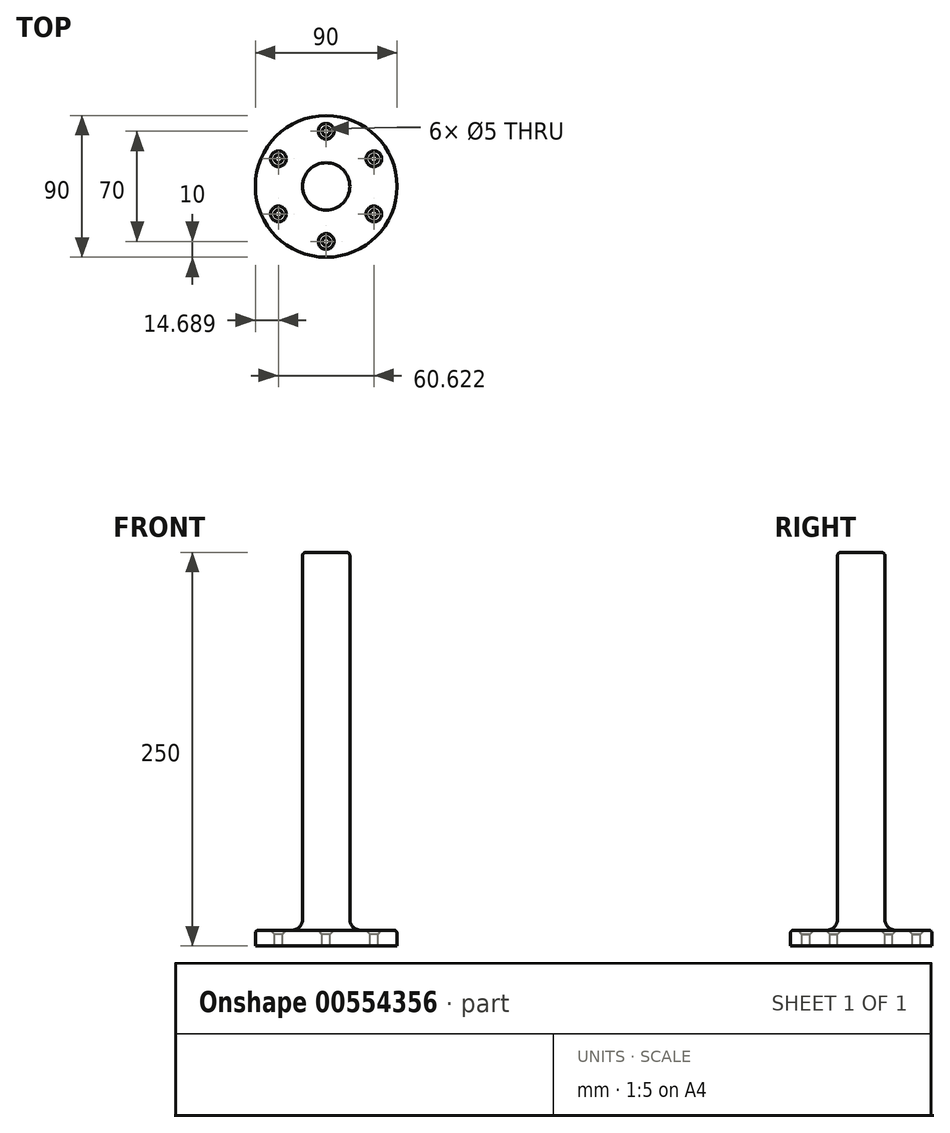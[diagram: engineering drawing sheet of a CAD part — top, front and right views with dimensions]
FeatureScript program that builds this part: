
annotation { "Feature Type Name" : "Feature", "Feature Type Description" : "" }
export const myFeature = defineFeature(function(context is Context, id is Id, definition is map)
    precondition{}
    {
        {
            var Q0;
            Q0=qCreatedBy(makeId("Top.planeOp"),FACE);
            var sketch = newSketch(context, id + "F0", { "sketchPlane" : qUnion([Q0])});
            skCircle(sketch, "E0", {"center": v(0, 0) * mm, "radius": 45 * mm});
            skSolve(sketch);
        }
        {
            var Q0;
            Q0=makeQuery(id+"F0.imprint","IMPRINT",FACE,{"disambiguationData":[TD([[makeQuery(id+"F0.imprint","IMPRINT",EDGE,{"derivedFrom":sQuery(id+"F0.wireOp",EDGE,"E0")}),1.0]])]});
            extrude(context, id + "F1", {"entities" : qUnion([Q0]), "depth" : 10 * mm, "offsetDistance" : 25.4 * mm});
        }
        {
            var Q0;
            Q0=qCreatedBy(makeId("Top.planeOp"),FACE);
            var sketch = newSketch(context, id + "F2", { "sketchPlane" : qUnion([Q0])});
            skCircle(sketch, "E1", {"center": v(0, 0) * mm, "radius": 15 * mm});
            skSolve(sketch);
        }
        {
            var Q0;
            Q0 = qSketchRegion(id + "F2", true);
            extrude(context, id + "F3", {"entities" : qUnion([Q0]), "operationType" : NewBodyOperationType.ADD, "depth" : 250 * mm, "offsetDistance" : 25 * mm});
        }
        {
            var Q0;
            Q0=makeQuery(id+"F1.opExtrude","CAP_FACE",FACE,{"disambiguationData":[OSD([sQuery(id+"F0.wireOp",EDGE,"E0")])],"isStart":false});
            var sketch = newSketch(context, id + "F4", { "sketchPlane" : qUnion([Q0])});
            skCircle(sketch, "E2", {"center": v(0, 35) * mm, "radius": 4.5 * mm});
            skCircle(sketch, "E3.1.0", {"center": v(-30.31, 17.5) * mm, "radius": 4.5 * mm});
            skCircle(sketch, "E3.2.0", {"center": v(-30.31, -17.5) * mm, "radius": 4.5 * mm});
            skCircle(sketch, "E3.3.0", {"center": v(0, -35) * mm, "radius": 4.5 * mm});
            skCircle(sketch, "E3.4.0", {"center": v(30.31, -17.5) * mm, "radius": 4.5 * mm});
            skCircle(sketch, "E3.5.0", {"center": v(30.31, 17.5) * mm, "radius": 4.5 * mm});
            skPoint(sketch, "E3.center", {"position": v(0, 0) * mm});
            skLineSegment(sketch, "E4", {"start": v(0, 0) * mm, "end": v(0, 35) * mm});
            skSolve(sketch);
        }
        {
            var Q0;
            Q0=sQuery(id+"F4.wireOp",VERTEX,"E2.center");
            var Q1;
            Q1=sQuery(id+"F4.wireOp",VERTEX,"E3.1.0.center");
            var Q2;
            Q2=sQuery(id+"F4.wireOp",VERTEX,"E3.2.0.center");
            var Q3;
            Q3=sQuery(id+"F4.wireOp",VERTEX,"E3.3.0.center");
            var Q4;
            Q4=sQuery(id+"F4.wireOp",VERTEX,"E3.4.0.center");
            var Q5;
            Q5=sQuery(id+"F4.wireOp",VERTEX,"E3.5.0.center");
            var Q6;
            Q6=makeQuery(id+"F1.opExtrude","SWEPT_BODY",BODY,{"disambiguationData":[OSD([sQuery(id+"F0.wireOp",EDGE,"E0")])]});
            hole(context, id + "F5", {"style" : HoleStyle.C_SINK, "endStyle" : HoleEndStyle.THROUGH, "holeDiameter" : 5 * mm, "cSinkDiameter" : 10 * mm, "cSinkAngle" : 90 * degree, "isTappedThrough" : true, "tappedDepth" : 12 * mm, "tapClearance" : 3, "locations" : qUnion([Q0, Q1, Q2, Q3, Q4, Q5]), "scope" : qUnion([Q6])});
        }
        {
            var Q0;
            Q0=makeQuery(id+"F3.boolean.opBoolean","INTERSECT",EDGE,{"derivedFrom":[makeQuery(id+"F1.opExtrude","CAP_FACE",FACE,{"disambiguationData":[OSD([sQuery(id+"F0.wireOp",EDGE,"E0")])],"isStart":false}),makeQuery(id+"F3.opExtrude","SWEPT_FACE",FACE,{"disambiguationData":[OSD([sQuery(id+"F2.wireOp",EDGE,"E1")])]})]});
            fillet(context, id + "F6", {"entities" : qUnion([Q0]), "radius" : 7 * mm, "tangentPropagation" : true, "allowEdgeOverflow" : false});
        }
        {
            var Q0;
            Q0=makeQuery(id+"F3.opExtrude","CAP_EDGE",EDGE,{"disambiguationData":[OSD([sQuery(id+"F2.wireOp",EDGE,"E1")])],"isStart":false});
            fillet(context, id + "F7", {"entities" : qUnion([Q0]), "radius" : 2 * mm, "tangentPropagation" : true, "allowEdgeOverflow" : false});
        }
        {
            var Q0;
            Q0=makeQuery(id+"F1.opExtrude","CAP_EDGE",EDGE,{"disambiguationData":[OSD([sQuery(id+"F0.wireOp",EDGE,"E0")])],"isStart":false});
            fillet(context, id + "F8", {"entities" : qUnion([Q0]), "radius" : 2 * mm, "tangentPropagation" : true, "allowEdgeOverflow" : false});
        }
    });
